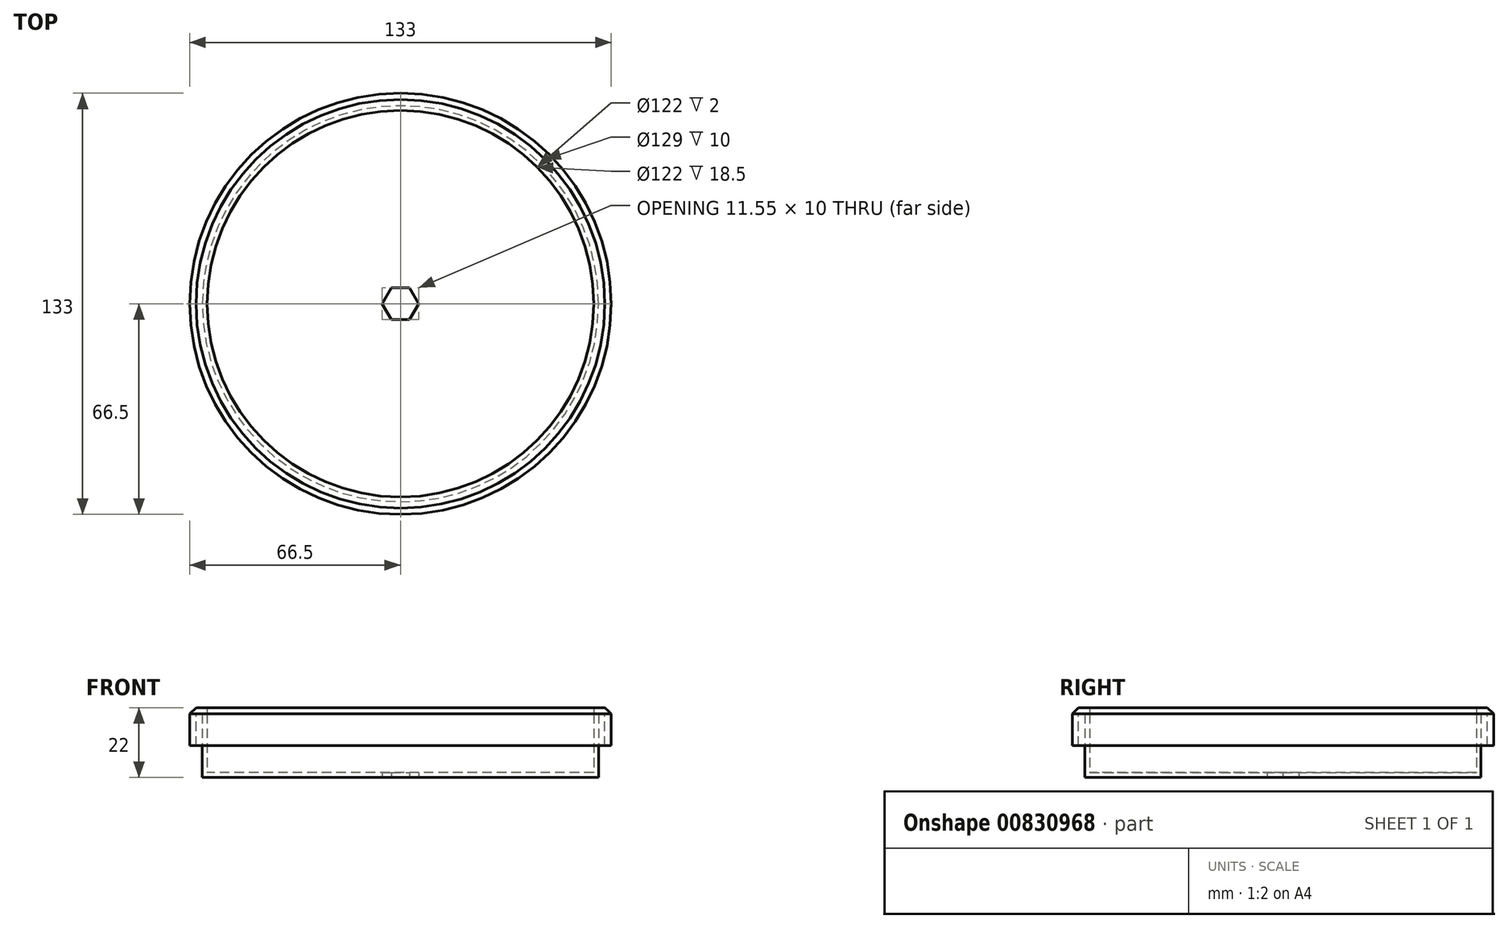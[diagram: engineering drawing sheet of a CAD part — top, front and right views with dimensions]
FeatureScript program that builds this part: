
annotation { "Feature Type Name" : "Feature", "Feature Type Description" : "" }
export const myFeature = defineFeature(function(context is Context, id is Id, definition is map)
    precondition{}
    {
        {
            var Q0;
            Q0=qCreatedBy(makeId("Top.planeOp"),FACE);
            var sketch = newSketch(context, id + "F0", { "sketchPlane" : qUnion([Q0])});
            skCircle(sketch, "E0", {"center": v(0, 0) * mm, "radius": 62.5 * mm});
            skCircle(sketch, "E1.cCircle", {"center": v(0, 0) * mm, "radius": 5 * mm, "construction": true});
            skLineSegment(sketch, "E1.0", {"start": v(2.89, -5) * mm, "end": v(-2.89, -5) * mm});
            skLineSegment(sketch, "E1.1", {"start": v(-2.89, -5) * mm, "end": v(-5.77, 0) * mm});
            skLineSegment(sketch, "E1.2", {"start": v(-5.77, 0) * mm, "end": v(-2.89, 5) * mm});
            skLineSegment(sketch, "E1.3", {"start": v(-2.89, 5) * mm, "end": v(2.89, 5) * mm});
            skLineSegment(sketch, "E1.4", {"start": v(2.89, 5) * mm, "end": v(5.77, 0) * mm});
            skLineSegment(sketch, "E1.5", {"start": v(5.77, 0) * mm, "end": v(2.89, -5) * mm});
            skPoint(sketch, "E1.0.midPoint", {"position": v(0, -5) * mm});
            skSolve(sketch);
        }
        {
            var Q0;
            Q0=makeQuery(id+"F0.imprint","IMPRINT",FACE,{"disambiguationData":[TD([[makeQuery(id+"F0.imprint","IMPRINT",EDGE,{"derivedFrom":sQuery(id+"F0.wireOp",EDGE,"E0")}),1.0]])]});
            var Q1;
            Q1=makeQuery(id+"F0.imprint","IMPRINT",FACE,{"disambiguationData":[TD([[makeQuery(id+"F0.imprint","IMPRINT",EDGE,{"derivedFrom":sQuery(id+"F0.wireOp",EDGE,"E1.0")}),-1.0]])]});
            extrude(context, id + "F1", {"entities" : qUnion([Q0, Q1]), "depth" : 20 * mm, "offsetDistance" : 25 * mm});
        }
        {
            var Q0;
            Q0=makeQuery(id+"F1.opExtrude","CAP_FACE",FACE,{"disambiguationData":[OSD([sQuery(id+"F0.wireOp",EDGE,"E0")])],"isStart":false});
            shell(context, id + "F2", {"entities" : qUnion([Q0]), "thickness" : 1.5 * mm});
        }
        {
            var Q0;
            Q0=makeQuery(id+"F0.imprint","IMPRINT",FACE,{"disambiguationData":[TD([[makeQuery(id+"F0.imprint","IMPRINT",EDGE,{"derivedFrom":sQuery(id+"F0.wireOp",EDGE,"E1.0")}),-1.0]])]});
            extrude(context, id + "F3", {"entities" : qUnion([Q0]), "operationType" : NewBodyOperationType.REMOVE, "depth" : 25 * mm, "offsetDistance" : 25 * mm});
        }
        {
            var Q0;
            Q0=makeQuery(id+"F1.opExtrude","CAP_FACE",FACE,{"disambiguationData":[OSD([sQuery(id+"F0.wireOp",EDGE,"E0")])],"isStart":false});
            var sketch = newSketch(context, id + "F4", { "sketchPlane" : qUnion([Q0])});
            skCircle(sketch, "E2.0", {"center": v(0, 0) * mm, "radius": 62.5 * mm, "construction": true});
            skCircle(sketch, "E3.0", {"center": v(0, 0) * mm, "radius": 64.5 * mm});
            skCircle(sketch, "E4.0", {"center": v(0, 0) * mm, "radius": 66.5 * mm});
            skCircle(sketch, "E5.0", {"center": v(0, 0) * mm, "radius": 61 * mm});
            skSolve(sketch);
        }
        {
            var Q0;
            Q0=qSketchRegion(id+"F4",true);
            var Q1;
            Q1=makeQuery(id+"F4.imprint","IMPRINT",FACE,{"disambiguationData":[TD([[makeQuery(id+"F4.imprint","IMPRINT",EDGE,{"derivedFrom":sQuery(id+"F4.wireOp",EDGE,"E3.0")}),1.0]])]});
            var Q2;
            Q2=makeQuery(id+"F4.imprint","IMPRINT",FACE,{"disambiguationData":[TD([[makeQuery(id+"F4.imprint","IMPRINT",EDGE,{"derivedFrom":sQuery(id+"F4.wireOp",EDGE,"E5.0")}),-1.0]])]});
            extrude(context, id + "F5", {"entities" : qUnion([Q0, Q1, Q2]), "depth" : 2 * mm, "offsetDistance" : 25 * mm});
        }
        {
            var Q0;
            Q0=makeQuery(id+"F4.imprint","IMPRINT",FACE,{"disambiguationData":[TD([[makeQuery(id+"F4.imprint","IMPRINT",EDGE,{"derivedFrom":sQuery(id+"F4.wireOp",EDGE,"E3.0")}),-1.0]])]});
            extrude(context, id + "F6", {"entities" : qUnion([Q0]), "operationType" : NewBodyOperationType.ADD, "oppositeDirection" : true, "depth" : 10 * mm, "offsetDistance" : 25 * mm});
        }
        {
            var Q0;
            Q0=makeQuery(id+"F5.opExtrude","CAP_EDGE",EDGE,{"disambiguationData":[OSD([sQuery(id+"F4.wireOp",EDGE,"E4.0")])],"isStart":false});
            chamfer(context, id + "F7", {"entities" : qUnion([Q0]), "width" : 2 * mm, "tangentPropagation" : true});
        }
    });
